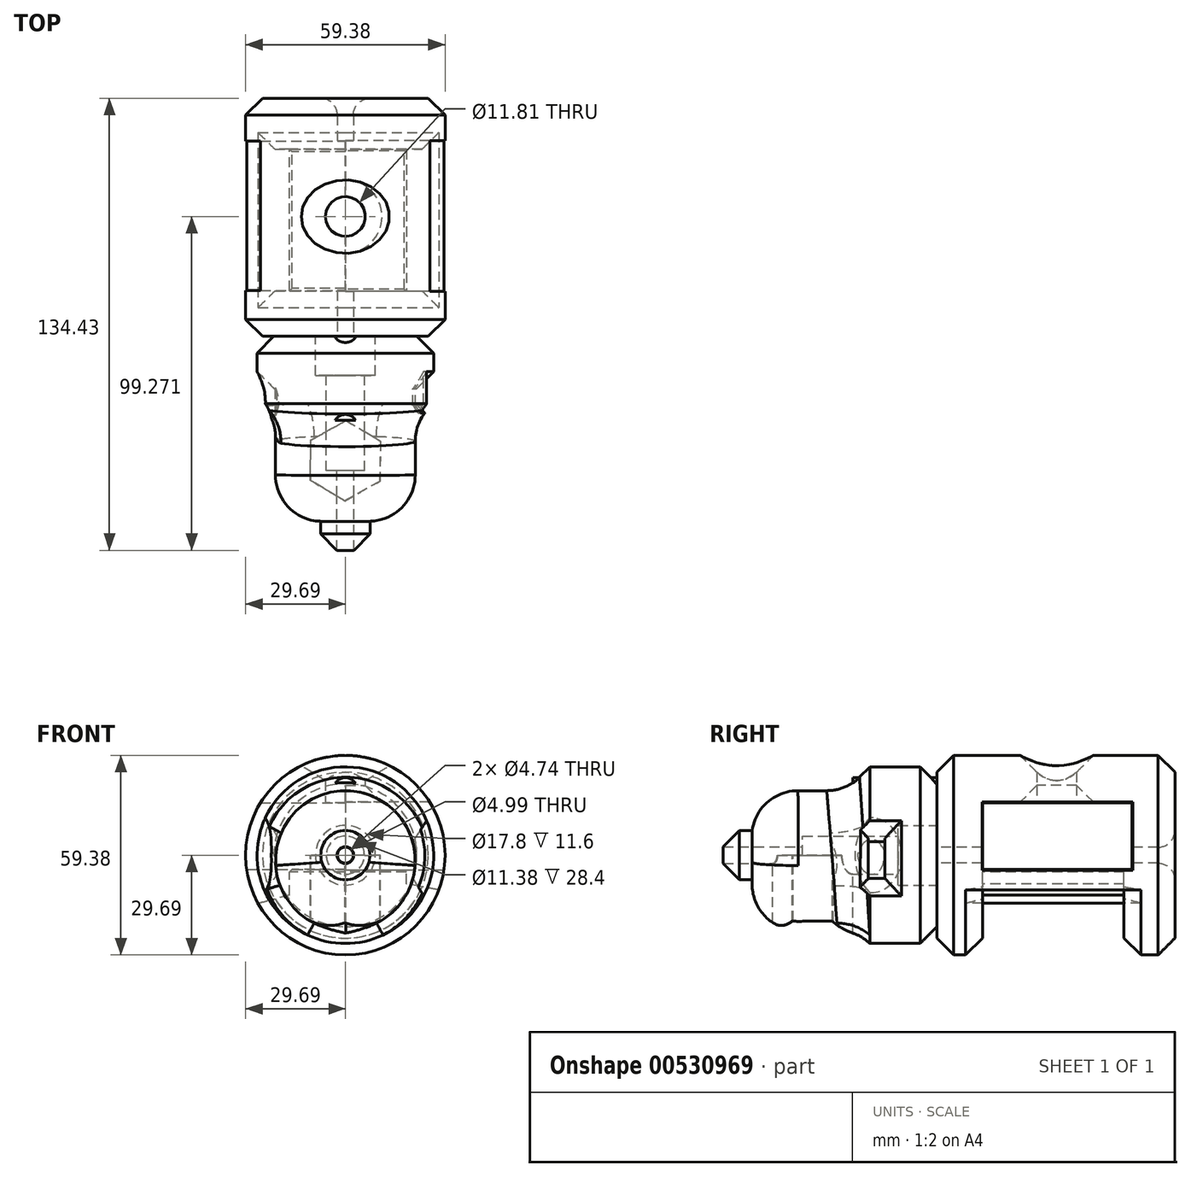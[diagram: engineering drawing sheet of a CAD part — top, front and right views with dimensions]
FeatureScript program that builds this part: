
annotation { "Feature Type Name" : "Feature", "Feature Type Description" : "" }
export const myFeature = defineFeature(function(context is Context, id is Id, definition is map)
    precondition{}
    {
        {
            var Q0;
            Q0=qCreatedBy(makeId("Front.planeOp"),FACE);
            var sketch = newSketch(context, id + "F0", { "sketchPlane" : qUnion([Q0])});
            skCircle(sketch, "E0", {"center": v(0, 0) * mm, "radius": 26.27 * mm});
            skSolve(sketch);
        }
        {
            var Q0;
            Q0=makeQuery(id+"F0.imprint","IMPRINT",FACE,{"disambiguationData":[TD([[makeQuery(id+"F0.imprint","IMPRINT",EDGE,{"derivedFrom":sQuery(id+"F0.wireOp",EDGE,"E0")}),1.0]])]});
            extrude(context, id + "F1", {"entities" : qUnion([Q0]), "depth" : 25 * mm, "offsetDistance" : 25 * mm});
        }
        {
            var Q0;
            Q0=makeQuery(id+"F1.opExtrude","CAP_FACE",FACE,{"disambiguationData":[OSD([sQuery(id+"F0.wireOp",EDGE,"E0")])],"isStart":false});
            var sketch = newSketch(context, id + "F2", { "sketchPlane" : qUnion([Q0])});
            skCircle(sketch, "E1", {"center": v(0, 0) * mm, "radius": 14.61 * mm});
            skSolve(sketch);
        }
        {
            var Q0;
            Q0=makeQuery(id+"F2.imprint","IMPRINT",FACE,{"disambiguationData":[TD([[makeQuery(id+"F2.imprint","IMPRINT",EDGE,{"derivedFrom":sQuery(id+"F2.wireOp",EDGE,"E1")}),1.0]])]});
            extrude(context, id + "F3", {"entities" : qUnion([Q0]), "operationType" : NewBodyOperationType.REMOVE, "oppositeDirection" : true, "depth" : 20 * mm, "offsetDistance" : 25 * mm});
        }
        {
            var Q0;
            Q0=qCreatedBy(makeId("Right.planeOp"),FACE);
            var sketch = newSketch(context, id + "F4", { "sketchPlane" : qUnion([Q0])});
            skCircle(sketch, "E2", {"center": v(-19.47, 0) * mm, "radius": 4.01 * mm});
            skSolve(sketch);
        }
        {
            var Q0;
            Q0 = qSketchRegion(id + "F4", true);
            extrude(context, id + "F5", {"entities" : qUnion([Q0]), "operationType" : NewBodyOperationType.REMOVE, "oppositeDirection" : true, "depth" : 5000 * mm, "offsetDistance" : 25 * mm});
        }
        {
            var Q0;
            Q0=qCreatedBy(makeId("Right.planeOp"),FACE);
            var sketch = newSketch(context, id + "F6", { "sketchPlane" : qUnion([Q0])});
            skLineSegment(sketch, "E3.bottom", {"start": v(-20.42, 3.3) * mm, "end": v(-15.5, 3.3) * mm});
            skLineSegment(sketch, "E3.top", {"start": v(-20.42, -4.82) * mm, "end": v(-15.5, -4.82) * mm});
            skLineSegment(sketch, "E3.left", {"start": v(-20.42, 3.3) * mm, "end": v(-20.42, -4.82) * mm});
            skLineSegment(sketch, "E3.right", {"start": v(-15.5, 3.3) * mm, "end": v(-15.5, -4.82) * mm});
            skSolve(sketch);
        }
        {
            var Q0;
            Q0 = qSketchRegion(id + "F6", true);
            extrude(context, id + "F7", {"entities" : qUnion([Q0]), "operationType" : NewBodyOperationType.REMOVE, "depth" : 38.9 * mm, "offsetDistance" : 25 * mm});
        }
        {
            var Q0;
            Q0=qCreatedBy(makeId("Front.planeOp"),FACE);
            var sketch = newSketch(context, id + "F8", { "sketchPlane" : qUnion([Q0])});
            skCircle(sketch, "E4", {"center": v(-20.8, 0) * mm, "radius": 3.25 * mm});
            skCircle(sketch, "E5", {"center": v(0, 19.53) * mm, "radius": 3.53 * mm});
            skCircle(sketch, "E6", {"center": v(19.47, 0) * mm, "radius": 3.16 * mm});
            skCircle(sketch, "E7", {"center": v(0, -21.12) * mm, "radius": 3.24 * mm});
            skSolve(sketch);
        }
        {
            var Q0;
            Q0=qCreatedBy(makeId("Front.planeOp"),FACE);
            var sketch = newSketch(context, id + "F9", { "sketchPlane" : qUnion([Q0])});
            skCircle(sketch, "E8", {"center": v(0, 0) * mm, "radius": 7.33 * mm});
            skSolve(sketch);
        }
        {
            var Q0;
            Q0 = qSketchRegion(id + "F9", true);
            extrude(context, id + "F10", {"entities" : qUnion([Q0]), "operationType" : NewBodyOperationType.ADD, "depth" : 63.8 * mm, "offsetDistance" : 25 * mm});
        }
        {
            var Q0;
            Q0=qCreatedBy(makeId("Front.planeOp"),FACE);
            var sketch = newSketch(context, id + "F11", { "sketchPlane" : qUnion([Q0])});
            skCircle(sketch, "E9", {"center": v(0, -1.6) * mm, "radius": 20.8 * mm});
            skSolve(sketch);
        }
        {
            var Q0;
            Q0 = qSketchRegion(id + "F11", true);
            extrude(context, id + "F12", {"entities" : qUnion([Q0]), "operationType" : NewBodyOperationType.ADD, "depth" : 55 * mm, "offsetDistance" : 25 * mm});
        }
        {
            var Q0;
            Q0=makeQuery(id+"F1.opExtrude","SWEPT_FACE",FACE,{"disambiguationData":[OSD([sQuery(id+"F0.wireOp",EDGE,"E0")])]});
            chamfer(context, id + "F13", {"entities" : qUnion([Q0]), "width" : 5 * mm, "tangentPropagation" : true});
        }
        {
            var Q0;
            {var subQ0=sQuery(id+"F11.wireOp",EDGE,"E9");Q0=makeQuery(id+"F12.boolean.opBoolean","SPLIT",FACE,{"disambiguationData":[TD([makeQuery(id+"F1.opExtrude","CAP_FACE",FACE,{"disambiguationData":[OSD([sQuery(id+"F0.wireOp",EDGE,"E0")])],"isStart":false})])],"derivedFrom":makeQuery(id+"F12.opExtrude","SWEPT_FACE",FACE,{"disambiguationData":[OSD([subQ0])]})});}
            fillet(context, id + "F14", {"entities" : qUnion([Q0]), "radius" : 13.76 * mm, "tangentPropagation" : true, "allowEdgeOverflow" : false});
        }
        {
            var Q0;
            Q0=makeQuery(id+"F10.opExtrude","CAP_EDGE",EDGE,{"disambiguationData":[OSD([sQuery(id+"F9.wireOp",EDGE,"E8")])],"isStart":false});
            chamfer(context, id + "F15", {"entities" : qUnion([Q0]), "width" : 5 * mm, "tangentPropagation" : true});
        }
        {
            var Q0;
            Q0=qCreatedBy(makeId("Front.planeOp"),FACE);
            var sketch = newSketch(context, id + "F16", { "sketchPlane" : qUnion([Q0])});
            skSolve(sketch);
        }
        {
            var Q0;
            Q0 = qSketchRegion(id + "F16", true);
            var Q1;
            Q1=makeQuery(id+"F8.imprint","IMPRINT",FACE,{"disambiguationData":[TD([[makeQuery(id+"F8.imprint","IMPRINT",EDGE,{"derivedFrom":sQuery(id+"F8.wireOp",EDGE,"E5")}),1.0]])]});
            extrude(context, id + "F17", {"entities" : qUnion([Q0, Q1]), "operationType" : NewBodyOperationType.ADD, "depth" : 25 * mm, "offsetDistance" : 25 * mm});
        }
        {
            var Q0;
            Q0=makeQuery(id+"F10.opExtrude","CAP_FACE",FACE,{"disambiguationData":[OSD([sQuery(id+"F9.wireOp",EDGE,"E8")])],"isStart":false});
            extrude(context, id + "F18", {"entities" : qUnion([Q0]), "operationType" : NewBodyOperationType.REMOVE, "oppositeDirection" : true, "depth" : 25 * mm, "offsetDistance" : 25 * mm});
        }
        {
            var Q0;
            Q0=qCreatedBy(makeId("Front.planeOp"),FACE);
            var sketch = newSketch(context, id + "F19", { "sketchPlane" : qUnion([Q0])});
            skPoint(sketch, "E10.center.orphan", {"position": v(0, -2.55) * mm});
            skCircle(sketch, "E11", {"center": v(0, 0) * mm, "radius": 5.7 * mm});
            skSolve(sketch);
        }
        {
            var Q0;
            Q0=makeQuery(id+"F19.imprint","IMPRINT",FACE,{"disambiguationData":[TD([[makeQuery(id+"F19.imprint","IMPRINT",EDGE,{"derivedFrom":sQuery(id+"F19.wireOp",EDGE,"E11")}),1.0]])]});
            extrude(context, id + "F20", {"entities" : qUnion([Q0]), "operationType" : NewBodyOperationType.REMOVE, "depth" : 40 * mm, "offsetDistance" : 25 * mm});
        }
        {
            var Q0;
            Q0=qCreatedBy(makeId("Front.planeOp"),FACE);
            var sketch = newSketch(context, id + "F21", { "sketchPlane" : qUnion([Q0])});
            skCircle(sketch, "E12", {"center": v(0, 0) * mm, "radius": 8.9 * mm});
            skSolve(sketch);
        }
        {
            var Q0;
            Q0 = qSketchRegion(id + "F21", true);
            extrude(context, id + "F22", {"entities" : qUnion([Q0]), "operationType" : NewBodyOperationType.REMOVE, "depth" : 11.6 * mm, "offsetDistance" : 25 * mm});
        }
        {
            var Q0;
            Q0=qCreatedBy(makeId("Front.planeOp"),FACE);
            var sketch = newSketch(context, id + "F23", { "sketchPlane" : qUnion([Q0])});
            skCircle(sketch, "E13", {"center": v(0, 0) * mm, "radius": 29.69 * mm});
            skSolve(sketch);
        }
        {
            var Q0;
            Q0 = qSketchRegion(id + "F23", true);
            extrude(context, id + "F24", {"entities" : qUnion([Q0]), "operationType" : NewBodyOperationType.ADD, "oppositeDirection" : true, "depth" : 70.8 * mm, "offsetDistance" : 25 * mm});
        }
        {
            var Q0;
            Q0=qCreatedBy(makeId("Front.planeOp"),FACE);
            var sketch = newSketch(context, id + "F25", { "sketchPlane" : qUnion([Q0])});
            skCircle(sketch, "E14", {"center": v(0, 0) * mm, "radius": 2.5 * mm});
            skSolve(sketch);
        }
        {
            var Q0;
            Q0=qCreatedBy(makeId("Top.planeOp"),FACE);
            var sketch = newSketch(context, id + "F26", { "sketchPlane" : qUnion([Q0])});
            skLineSegment(sketch, "E15.bottom", {"start": v(-16.64, 55.68) * mm, "end": v(18.15, 55.68) * mm});
            skLineSegment(sketch, "E15.top", {"start": v(-16.64, 13.52) * mm, "end": v(18.15, 13.52) * mm});
            skLineSegment(sketch, "E15.left", {"start": v(-16.64, 55.68) * mm, "end": v(-16.64, 13.52) * mm});
            skLineSegment(sketch, "E15.right", {"start": v(18.15, 55.68) * mm, "end": v(18.15, 13.52) * mm});
            skSolve(sketch);
        }
        {
            var Q0;
            Q0 = qSketchRegion(id + "F26", true);
            extrude(context, id + "F27", {"entities" : qUnion([Q0]), "operationType" : NewBodyOperationType.REMOVE, "oppositeDirection" : true, "depth" : 41.5 * mm, "offsetDistance" : 25 * mm});
        }
        {
            var Q0;
            Q0=makeQuery(id+"F27.boolean.opBoolean","COPY",FACE,{"derivedFrom":makeQuery(id+"F27.opExtrude","CAP_FACE",FACE,{"disambiguationData":[OSD([sQuery(id+"F26.wireOp",EDGE,"E15.bottom"),sQuery(id+"F26.wireOp",EDGE,"E15.top"),sQuery(id+"F26.wireOp",EDGE,"E15.left"),sQuery(id+"F26.wireOp",EDGE,"E15.right")])],"isStart":true})});
            var Q1;
            Q1=makeQuery(id+"F24.opExtrude","SWEPT_FACE",FACE,{"disambiguationData":[OSD([sQuery(id+"F23.wireOp",EDGE,"E13")])]});
            chamfer(context, id + "F28", {"entities" : qUnion([Q0, Q1]), "width" : 5 * mm, "tangentPropagation" : true});
        }
        {
            var Q0;
            Q0=qCreatedBy(makeId("Top.planeOp"),FACE);
            var sketch = newSketch(context, id + "F29", { "sketchPlane" : qUnion([Q0])});
            skCircle(sketch, "E16", {"center": v(0, 35.64) * mm, "radius": 5.9 * mm});
            skSolve(sketch);
        }
        {
            var Q0;
            Q0=makeQuery(id+"F29.imprint","IMPRINT",FACE,{"disambiguationData":[TD([[makeQuery(id+"F29.imprint","IMPRINT",EDGE,{"derivedFrom":sQuery(id+"F29.wireOp",EDGE,"E16")}),1.0]])]});
            extrude(context, id + "F30", {"entities" : qUnion([Q0]), "operationType" : NewBodyOperationType.REMOVE, "depth" : 50.9 * mm, "offsetDistance" : 25 * mm});
        }
        {
            var Q0;
            Q0=qCreatedBy(makeId("Front.planeOp"),FACE);
            var sketch = newSketch(context, id + "F31", { "sketchPlane" : qUnion([Q0])});
            skCircle(sketch, "E17", {"center": v(0, 0) * mm, "radius": 2.07 * mm});
            skSolve(sketch);
        }
        {
            var Q0;
            Q0 = qSketchRegion(id + "F31", true);
            var Q1;
            Q1=makeQuery(id+"F25.imprint","IMPRINT",FACE,{"disambiguationData":[TD([[makeQuery(id+"F25.imprint","IMPRINT",EDGE,{"derivedFrom":sQuery(id+"F25.wireOp",EDGE,"E14")}),1.0]])]});
            extrude(context, id + "F32", {"entities" : qUnion([Q0, Q1]), "operationType" : NewBodyOperationType.REMOVE, "depth" : 87.4 * mm, "offsetDistance" : 25 * mm});
        }
        {
            var Q0;
            Q0=qCreatedBy(makeId("Front.planeOp"),FACE);
            var sketch = newSketch(context, id + "F33", { "sketchPlane" : qUnion([Q0])});
            skCircle(sketch, "E18", {"center": v(0, 0) * mm, "radius": 2.37 * mm});
            skSolve(sketch);
        }
        {
            var Q0;
            Q0=qCreatedBy(makeId("Front.planeOp"),FACE);
            var sketch = newSketch(context, id + "F34", { "sketchPlane" : qUnion([Q0])});
            skCircle(sketch, "E19", {"center": v(0, 0) * mm, "radius": 2.34 * mm});
            skSolve(sketch);
        }
        {
            var Q0;
            Q0 = qSketchRegion(id + "F34", true);
            var Q1;
            Q1=makeQuery(id+"F33.imprint","IMPRINT",FACE,{"disambiguationData":[TD([[makeQuery(id+"F33.imprint","IMPRINT",EDGE,{"derivedFrom":sQuery(id+"F33.wireOp",EDGE,"E18")}),1.0]])]});
            extrude(context, id + "F35", {"entities" : qUnion([Q0, Q1]), "operationType" : NewBodyOperationType.REMOVE, "oppositeDirection" : true, "depth" : 122.7 * mm, "offsetDistance" : 25 * mm});
        }
        {
            var Q0;
            Q0=qCreatedBy(makeId("Right.planeOp"),FACE);
            var sketch = newSketch(context, id + "F36", { "sketchPlane" : qUnion([Q0])});
            skLineSegment(sketch, "E20.bottom", {"start": v(13.61, 15.6) * mm, "end": v(58.05, 15.6) * mm});
            skLineSegment(sketch, "E20.top", {"start": v(13.61, -4.25) * mm, "end": v(58.05, -4.25) * mm});
            skLineSegment(sketch, "E20.left", {"start": v(13.61, 15.6) * mm, "end": v(13.61, -4.25) * mm});
            skLineSegment(sketch, "E20.right", {"start": v(58.05, 15.6) * mm, "end": v(58.05, -4.25) * mm});
            skSolve(sketch);
        }
        {
            var Q0;
            Q0 = qSketchRegion(id + "F36", true);
            extrude(context, id + "F37", {"entities" : qUnion([Q0]), "operationType" : NewBodyOperationType.REMOVE, "oppositeDirection" : true, "depth" : 48.8 * mm, "offsetDistance" : 25 * mm});
        }
        {
            var Q0;
            Q0=qCreatedBy(makeId("Right.planeOp"),FACE);
            var sketch = newSketch(context, id + "F38", { "sketchPlane" : qUnion([Q0])});
            skLineSegment(sketch, "E21.bottom", {"start": v(58.24, 15.79) * mm, "end": v(13.42, 15.79) * mm});
            skLineSegment(sketch, "E21.top", {"start": v(58.24, -4.44) * mm, "end": v(13.42, -4.44) * mm});
            skLineSegment(sketch, "E21.left", {"start": v(58.24, 15.79) * mm, "end": v(58.24, -4.44) * mm});
            skLineSegment(sketch, "E21.right", {"start": v(13.42, 15.79) * mm, "end": v(13.42, -4.44) * mm});
            skSolve(sketch);
        }
        {
            var Q0;
            Q0 = qSketchRegion(id + "F38", true);
            extrude(context, id + "F39", {"entities" : qUnion([Q0]), "operationType" : NewBodyOperationType.REMOVE, "depth" : 43.8 * mm, "offsetDistance" : 25 * mm});
        }
        {
            var Q0;
            Q0=qCreatedBy(makeId("Top.planeOp"),FACE);
            var sketch = newSketch(context, id + "F40", { "sketchPlane" : qUnion([Q0])});
            skCircle(sketch, "E22.cCircle", {"center": v(0, -36.96) * mm, "radius": 10.34 * mm, "construction": true});
            skLineSegment(sketch, "E22.0", {"start": v(0.16, -25.02) * mm, "end": v(10.42, -31.13) * mm});
            skLineSegment(sketch, "E22.1", {"start": v(10.42, -31.13) * mm, "end": v(10.26, -43.08) * mm});
            skLineSegment(sketch, "E22.2", {"start": v(10.26, -43.08) * mm, "end": v(-0.16, -48.9) * mm});
            skLineSegment(sketch, "E22.3", {"start": v(-0.16, -48.9) * mm, "end": v(-10.42, -42.8) * mm});
            skLineSegment(sketch, "E22.4", {"start": v(-10.42, -42.8) * mm, "end": v(-10.26, -30.85) * mm});
            skLineSegment(sketch, "E22.5", {"start": v(-10.26, -30.85) * mm, "end": v(0.16, -25.02) * mm});
            skPoint(sketch, "E22.0.midPoint", {"position": v(5.3, -28.08) * mm});
            skSolve(sketch);
        }
        {
            var Q0;
            Q0 = qSketchRegion(id + "F40", true);
            extrude(context, id + "F41", {"entities" : qUnion([Q0]), "operationType" : NewBodyOperationType.REMOVE, "oppositeDirection" : true, "depth" : 25 * mm, "offsetDistance" : 25 * mm});
        }
        {
            var Q0;
            Q0=makeQuery(id+"F39.boolean.opBoolean","INTERSECT",EDGE,{"derivedFrom":[makeQuery(id+"F30.boolean.opBoolean","COPY",FACE,{"derivedFrom":makeQuery(id+"F30.opExtrude","SWEPT_FACE",FACE,{"disambiguationData":[OSD([sQuery(id+"F29.wireOp",EDGE,"E16")])]})}),makeQuery(id+"F39.opExtrude","SWEPT_FACE",FACE,{"disambiguationData":[OSD([sQuery(id+"F38.wireOp",EDGE,"E21.bottom")])]})]});
            var Q1;
            Q1=makeQuery(id+"F30.boolean.opBoolean","INTERSECT",EDGE,{"derivedFrom":[makeQuery(id+"F24.opExtrude","SWEPT_FACE",FACE,{"disambiguationData":[OSD([sQuery(id+"F23.wireOp",EDGE,"E13")])]}),makeQuery(id+"F30.opExtrude","SWEPT_FACE",FACE,{"disambiguationData":[OSD([sQuery(id+"F29.wireOp",EDGE,"E16")])]})]});
            chamfer(context, id + "F42", {"entities" : qUnion([Q0, Q1]), "width" : 5 * mm, "tangentPropagation" : true});
        }
        {
            var Q0;
            Q0=makeQuery(id+"F35.boolean.opBoolean","INTERSECT",EDGE,{"derivedFrom":[makeQuery(id+"F24.opExtrude","CAP_FACE",FACE,{"disambiguationData":[OSD([sQuery(id+"F23.wireOp",EDGE,"E13")])],"isStart":false}),makeQuery(id+"F35.opExtrude","SWEPT_FACE",FACE,{"disambiguationData":[OSD([sQuery(id+"F33.wireOp",EDGE,"E18")])]})]});
            fillet(context, id + "F43", {"entities" : qUnion([Q0]), "radius" : 5 * mm, "tangentPropagation" : true, "allowEdgeOverflow" : false});
        }
    });
